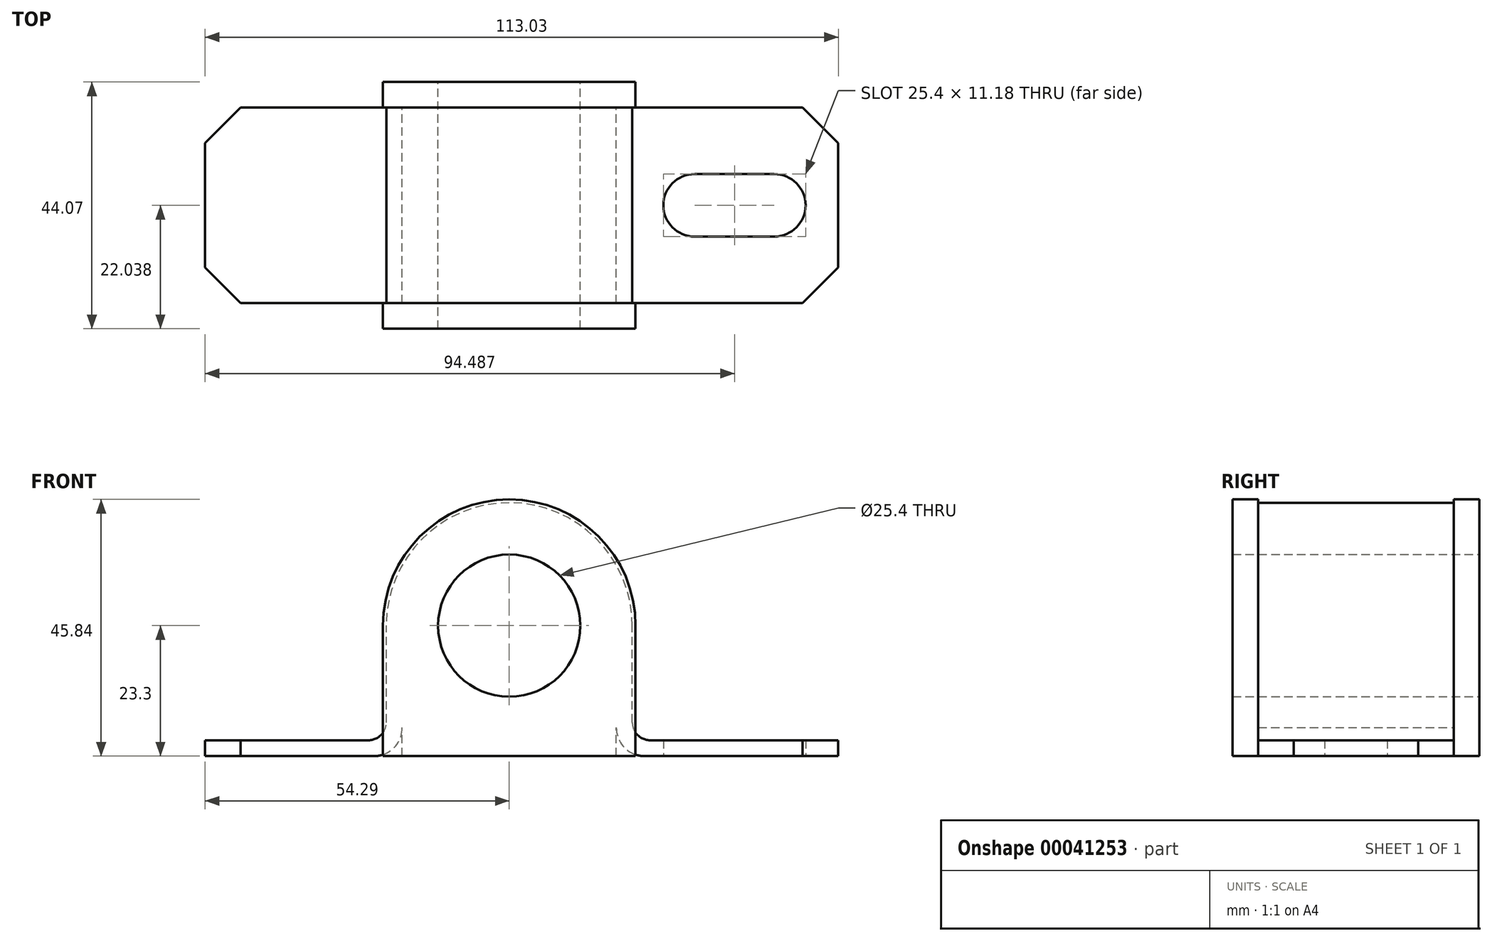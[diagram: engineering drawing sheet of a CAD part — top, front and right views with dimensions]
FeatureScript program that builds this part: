
annotation { "Feature Type Name" : "Feature", "Feature Type Description" : "" }
export const myFeature = defineFeature(function(context is Context, id is Id, definition is map)
    precondition{}
    {
        {
            var Q0;
            Q0=qCreatedBy(makeId("Front.planeOp"),FACE);
            var sketch = newSketch(context, id + "F0", { "sketchPlane" : qUnion([Q0])});
            skArc(sketch, "E0", {"start": v(19.11, 0) * mm, "mid": v(0, 19.11) * mm, "end": v(-19.11, 0) * mm});
            skLineSegment(sketch, "E1", {"start": v(-19.11, -23.3) * mm, "end": v(19.11, -23.3) * mm});
            skLineSegment(sketch, "E2", {"start": v(19.11, -23.3) * mm, "end": v(19.11, 0) * mm});
            skLineSegment(sketch, "E3", {"start": v(-19.11, -23.3) * mm, "end": v(-19.11, 0) * mm});
            skCircle(sketch, "E4", {"center": v(0, 0) * mm, "radius": 12.7 * mm});
            skSolve(sketch);
        }
        {
            var Q0;
            Q0=qCreatedBy(makeId("Front.planeOp"),FACE);
            var sketch = newSketch(context, id + "F1", { "sketchPlane" : qUnion([Q0])});
            skLineSegment(sketch, "E5.0", {"start": v(19.11, -23.3) * mm, "end": v(19.11, 0) * mm, "construction": true});
            skArc(sketch, "E6.0", {"start": v(19.11, 0) * mm, "mid": v(0, 19.11) * mm, "end": v(-19.11, 0) * mm, "construction": true});
            skLineSegment(sketch, "E7.0", {"start": v(-19.11, -23.3) * mm, "end": v(-19.11, 0) * mm, "construction": true});
            skLineSegment(sketch, "E8.0", {"start": v(-22.54, -23.3) * mm, "end": v(22.54, -23.3) * mm});
            skLineSegment(sketch, "E9.0", {"start": v(22.54, -23.3) * mm, "end": v(22.54, 0) * mm});
            skArc(sketch, "E9.1", {"start": v(22.54, 0) * mm, "mid": v(0, 22.54) * mm, "end": v(-22.54, 0) * mm});
            skLineSegment(sketch, "E9.2", {"start": v(-22.54, -23.3) * mm, "end": v(-22.54, 0) * mm});
            skPoint(sketch, "E10.orphan", {"position": v(-19.11, -23.3) * mm});
            skPoint(sketch, "E11.orphan", {"position": v(19.11, -23.3) * mm});
            skSolve(sketch);
        }
        {
            var Q0;
            {var subQ0=sQuery(id+"F0.wireOp",EDGE,"E3");Q0=makeQuery(id+"F0.imprint","IMPRINT",FACE,{"disambiguationData":[TD([[makeQuery(id+"F0.imprint","IMPRINT",EDGE,{"derivedFrom":subQ0}),-1.0]])]});}
            var Q1;
            {var subQ0=sQuery(id+"F0.wireOp",EDGE,"E2");Q1=makeQuery(id+"F0.imprint","IMPRINT",FACE,{"disambiguationData":[TD([[makeQuery(id+"F0.imprint","IMPRINT",EDGE,{"derivedFrom":subQ0}),1.0]])]});}
            var Q2;
            Q2=makeQuery(id+"F0.imprint","IMPRINT",FACE,{"disambiguationData":[TD([[makeQuery(id+"F0.imprint","IMPRINT",EDGE,{"derivedFrom":sQuery(id+"F0.wireOp",EDGE,"E4")}),-1.0]])]});
            extrude(context, id + "F2", {"entities" : qUnion([Q0, Q1, Q2]), "depth" : 34.92 * mm});
        }
        {
            var Q0;
            Q0=qCreatedBy(makeId("Front.planeOp"),FACE);
            var sketch = newSketch(context, id + "F3", { "sketchPlane" : qUnion([Q0])});
            skLineSegment(sketch, "E12.0", {"start": v(19.11, -23.3) * mm, "end": v(19.11, 0) * mm});
            skArc(sketch, "E13.0", {"start": v(19.11, 0) * mm, "mid": v(0, 19.11) * mm, "end": v(-19.11, 0) * mm});
            skLineSegment(sketch, "E14.0", {"start": v(-19.11, -23.3) * mm, "end": v(-19.11, 0) * mm});
            skLineSegment(sketch, "E15", {"start": v(-19.11, -23.3) * mm, "end": v(-54.3, -23.3) * mm});
            skLineSegment(sketch, "E16", {"start": v(19.11, -23.3) * mm, "end": v(58.74, -23.3) * mm});
            skLineSegment(sketch, "E17.0", {"start": v(-21.96, -20.46) * mm, "end": v(-54.3, -20.46) * mm});
            skLineSegment(sketch, "E17.1", {"start": v(-21.96, -20.46) * mm, "end": v(-21.96, 0) * mm});
            skArc(sketch, "E17.2", {"start": v(21.96, 0) * mm, "mid": v(0, 21.96) * mm, "end": v(-21.96, 0) * mm});
            skLineSegment(sketch, "E17.3", {"start": v(21.96, -20.46) * mm, "end": v(21.96, 0) * mm});
            skLineSegment(sketch, "E17.4", {"start": v(21.96, -20.46) * mm, "end": v(58.74, -20.46) * mm});
            skLineSegment(sketch, "E18", {"start": v(58.74, -20.46) * mm, "end": v(58.74, -23.3) * mm});
            skLineSegment(sketch, "E19", {"start": v(-54.3, -20.46) * mm, "end": v(-54.3, -23.3) * mm});
            skSolve(sketch);
        }
        {
            var Q0;
            Q0=qSketchRegion(id+"F1",true);
            extrude(context, id + "F4", {"entities" : qUnion([Q0]), "operationType" : NewBodyOperationType.ADD, "oppositeDirection" : true, "depth" : 4.57 * mm});
        }
        {
            var Q0;
            Q0=makeQuery(id+"F3.imprint","IMPRINT",FACE,{"disambiguationData":[TD([[makeQuery(id+"F3.imprint","IMPRINT",EDGE,{"derivedFrom":sQuery(id+"F3.wireOp",EDGE,"E12.0")}),-1.0]])]});
            var Q1;
            Q1=makeQuery(id+"F2.opExtrude","CAP_FACE",FACE,{"disambiguationData":[OSD([sQuery(id+"F0.wireOp",EDGE,"E0"),sQuery(id+"F0.wireOp",EDGE,"E1"),sQuery(id+"F0.wireOp",EDGE,"E2"),sQuery(id+"F0.wireOp",EDGE,"E3"),sQuery(id+"F0.wireOp",EDGE,"E4")])],"isStart":false});
            extrude(context, id + "F5", {"entities" : qUnion([Q0]), "endBound" : BoundingType.UP_TO_SURFACE, "endBoundEntityFace" : qUnion([Q1]), "depth" : 25.4 * mm});
        }
        {
            var Q0;
            Q0=makeQuery(id+"F5.opExtrude","SWEPT_EDGE",EDGE,{"disambiguationData":[OSD([sQuery(id+"F3.wireOp",EDGE,"E17.0"),sQuery(id+"F3.wireOp",EDGE,"E17.1")])]});
            var Q1;
            Q1=makeQuery(id+"F5.opExtrude","SWEPT_EDGE",EDGE,{"disambiguationData":[OSD([sQuery(id+"F3.wireOp",EDGE,"E17.3"),sQuery(id+"F3.wireOp",EDGE,"E17.4")])]});
            fillet(context, id + "F6", {"entities" : qUnion([Q0, Q1]), "radius" : 3.17 * mm, "tangentPropagation" : true, "allowEdgeOverflow" : false});
        }
        {
            var Q0;
            Q0=makeQuery(id+"F5.opExtrude","SWEPT_EDGE",EDGE,{"disambiguationData":[OSD([sQuery(id+"F3.wireOp",EDGE,"E14.0"),sQuery(id+"F3.wireOp",EDGE,"E15")])]});
            var Q1;
            Q1=makeQuery(id+"F5.opExtrude","SWEPT_EDGE",EDGE,{"disambiguationData":[OSD([sQuery(id+"F3.wireOp",EDGE,"E12.0"),sQuery(id+"F3.wireOp",EDGE,"E16")])]});
            fillet(context, id + "F7", {"entities" : qUnion([Q0, Q1]), "radius" : 5.08 * mm, "tangentPropagation" : true, "allowEdgeOverflow" : false});
        }
        {
            var Q0;
            Q0=makeQuery(id+"F5.opExtrude","SWEPT_FACE",FACE,{"disambiguationData":[OSD([sQuery(id+"F3.wireOp",EDGE,"E16")])]});
            var sketch = newSketch(context, id + "F8", { "sketchPlane" : qUnion([Q0])});
            skLineSegment(sketch, "E20", {"start": v(47.3, 11.87) * mm, "end": v(33.09, 11.87) * mm});
            skLineSegment(sketch, "E21", {"start": v(47.3, 23.05) * mm, "end": v(33.09, 23.05) * mm});
            skArc(sketch, "E22", {"start": v(47.3, 11.87) * mm, "mid": v(52.9, 17.46) * mm, "end": v(47.3, 23.05) * mm});
            skArc(sketch, "E23", {"start": v(33.09, 11.87) * mm, "mid": v(27.5, 17.46) * mm, "end": v(33.09, 23.05) * mm});
            skArc(sketch, "E24.MirrorCS", {"start": v(-43.37, 11.87) * mm, "mid": v(-48.96, 17.46) * mm, "end": v(-43.37, 23.05) * mm});
            skLineSegment(sketch, "E25", {"start": v(-43.37, 23.05) * mm, "end": v(-29.15, 23.05) * mm});
            skLineSegment(sketch, "E26", {"start": v(-43.37, 11.87) * mm, "end": v(-29.15, 11.87) * mm});
            skArc(sketch, "E27", {"start": v(-29.15, 11.87) * mm, "mid": v(-23.56, 17.46) * mm, "end": v(-29.15, 23.05) * mm});
            skLineSegment(sketch, "E28", {"start": v(-79.1, 17.46) * mm, "end": v(58.74, 17.46) * mm});
            skPoint(sketch, "E29.orphan", {"position": v(-28.56, 23.05) * mm});
            skPoint(sketch, "E30.orphan", {"position": v(-28.56, 11.87) * mm});
            skSolve(sketch);
        }
        {
            var Q0;
            Q0=makeQuery(id+"F8.imprint","IMPRINT",FACE,{"disambiguationData":[TD([[makeQuery(id+"F8.imprint","IMPRINT",EDGE,{"derivedFrom":sQuery(id+"F8.wireOp",EDGE,"E24.MirrorCS")}),-1.0]])]});
            var Q1;
            {var subQ5=sQuery(id+"F8.wireOp",EDGE,"E20");Q1=makeQuery(id+"F8.imprint","IMPRINT",FACE,{"disambiguationData":[TD([[makeQuery(id+"F8.imprint","IMPRINT",EDGE,{"derivedFrom":subQ5}),-1.0]])]});}
            var Q2;
            {var subQ5=sQuery(id+"F8.wireOp",EDGE,"E21");Q2=makeQuery(id+"F8.imprint","IMPRINT",FACE,{"disambiguationData":[TD([[makeQuery(id+"F8.imprint","IMPRINT",EDGE,{"derivedFrom":subQ5}),1.0]])]});}
            var Q3;
            Q3=makeQuery(id+"F5.opExtrude","SWEPT_FACE",FACE,{"disambiguationData":[OSD([sQuery(id+"F3.wireOp",EDGE,"E17.0")])]});
            extrude(context, id + "F9", {"entities" : qUnion([Q0, Q1, Q2]), "operationType" : NewBodyOperationType.REMOVE, "endBound" : BoundingType.THROUGH_ALL, "oppositeDirection" : true, "endBoundEntityFace" : qUnion([Q3]), "depth" : 25 * mm});
        }
        {
            var Q0;
            Q0=makeQuery(id+"F5.opExtrude","CAP_EDGE",EDGE,{"disambiguationData":[OSD([sQuery(id+"F3.wireOp",EDGE,"E19")])],"isStart":false});
            var Q1;
            Q1=makeQuery(id+"F5.opExtrude","CAP_EDGE",EDGE,{"disambiguationData":[OSD([sQuery(id+"F3.wireOp",EDGE,"E18")])],"isStart":false});
            var Q2;
            Q2=makeQuery(id+"F5.opExtrude","CAP_EDGE",EDGE,{"disambiguationData":[OSD([sQuery(id+"F3.wireOp",EDGE,"E19")])],"isStart":true});
            var Q3;
            Q3=makeQuery(id+"F5.opExtrude","CAP_EDGE",EDGE,{"disambiguationData":[OSD([sQuery(id+"F3.wireOp",EDGE,"E18")])],"isStart":true});
            chamfer(context, id + "F10", {"entities" : qUnion([Q0, Q1, Q2, Q3]), "width" : 6.35 * mm, "tangentPropagation" : true});
        }
        {
            var Q0;
            Q0=makeQuery(id+"F2.opExtrude","CAP_FACE",FACE,{"disambiguationData":[OSD([sQuery(id+"F0.wireOp",EDGE,"E0"),sQuery(id+"F0.wireOp",EDGE,"E1"),sQuery(id+"F0.wireOp",EDGE,"E2"),sQuery(id+"F0.wireOp",EDGE,"E3")])],"isStart":false});
            var sketch = newSketch(context, id + "F11", { "sketchPlane" : qUnion([Q0])});
            skLineSegment(sketch, "E31.0", {"start": v(-22.54, -23.3) * mm, "end": v(-22.54, 0) * mm});
            skArc(sketch, "E32.0", {"start": v(22.54, 0) * mm, "mid": v(0, 22.54) * mm, "end": v(-22.54, 0) * mm});
            skLineSegment(sketch, "E33.0", {"start": v(22.54, -23.3) * mm, "end": v(22.54, 0) * mm});
            skLineSegment(sketch, "E34.0", {"start": v(-22.54, -23.3) * mm, "end": v(22.54, -23.3) * mm});
            skSolve(sketch);
        }
        {
            var Q0;
            Q0=qSketchRegion(id+"F11",true);
            extrude(context, id + "F12", {"entities" : qUnion([Q0]), "operationType" : NewBodyOperationType.ADD, "depth" : 4.57 * mm});
        }
        {
            var Q0;
            Q0=makeQuery(id+"F4.opExtrude","CAP_FACE",FACE,{"disambiguationData":[OSD([sQuery(id+"F1.wireOp",EDGE,"E8.0"),sQuery(id+"F1.wireOp",EDGE,"E9.0"),sQuery(id+"F1.wireOp",EDGE,"E9.1"),sQuery(id+"F1.wireOp",EDGE,"E9.2")])],"isStart":false});
            var sketch = newSketch(context, id + "F13", { "sketchPlane" : qUnion([Q0])});
            skCircle(sketch, "E35.0", {"center": v(0, 0) * mm, "radius": 12.7 * mm});
            skSolve(sketch);
        }
        {
            var Q0;
            Q0=qSketchRegion(id+"F13",true);
            extrude(context, id + "F14", {"entities" : qUnion([Q0]), "operationType" : NewBodyOperationType.REMOVE, "endBound" : BoundingType.THROUGH_ALL, "oppositeDirection" : true, "depth" : 25 * mm});
        }
    });
